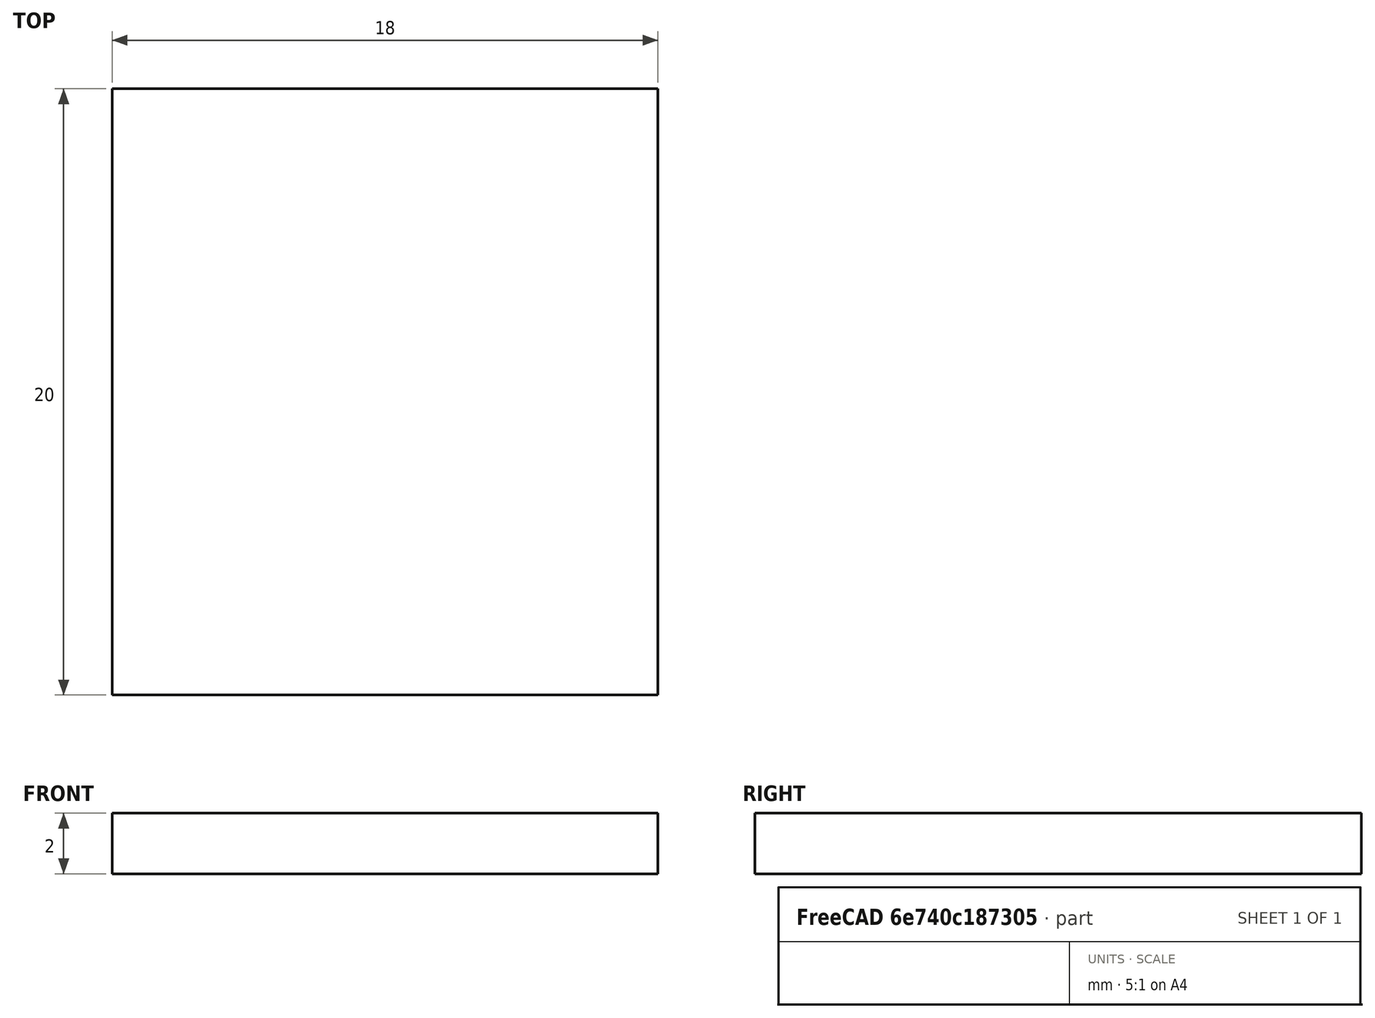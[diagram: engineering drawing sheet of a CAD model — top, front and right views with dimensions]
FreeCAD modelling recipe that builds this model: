
FCSTD DOCUMENT  (FreeCAD 0.16R6706 (Git))
Label: iROB-EA_Modulo_Sensores_Tapa_Cable_Servo
License: All rights reserved
LicenseURL: http://en.wikipedia.org/wiki/All_rights_reserved
objects: Sketcher::SketchObject×1, PartDesign::Pad×1
note: 3 computed .brp shape members not serialized (recipe doc carries the construction recipe); baked Part::Feature solids carry a one-line shape summary decoded from their .brp

FEATURE [Sketcher::SketchObject] Sketch  label="Base"
  sketch-geometry (4):
    g0: LineSegment StartX=0 StartY=20 StartZ=0 EndX=18 EndY=20 EndZ=0
    g1: LineSegment StartX=18 StartY=20 StartZ=0 EndX=18 EndY=0 EndZ=0
    g2: LineSegment StartX=18 StartY=0 StartZ=0 EndX=0 EndY=0 EndZ=0
    g3: LineSegment StartX=0 StartY=0 StartZ=0 EndX=0 EndY=20 EndZ=0
  constraints (11):
    c: Coincident(g0,g1)
    c: Coincident(g1,g2)
    c: Coincident(g2,g3)
    c: Coincident(g3,g0)
    c: Horizontal(g0)
    c: Horizontal(g2)
    c: Vertical(g1)
    c: Vertical(g3)
    c: DistanceX(g0,g0) = 18
    c: DistanceY(g3,g3) = 20
    c: Coincident(g2,g-1)
FEATURE [PartDesign::Pad] Pad
  Length = 2
  Length2 = 100
  Sketch = -> Sketch
  Type = 0
